# Revit family: Hager-Gamma-IP30-syst-NoHosted-CH-fr
name_source: partatom
category: Electrical Equipment
units: mm (PartAtom-declared; Revit-internal decimal feet)

## family parameters
Always vertical = Yes
Cut with Voids When Loaded = No
Panel Configuration = Two Columns, Circuits Across
Part Type = Panelboard
Room Calculation Point = No
Round Connector Dimension = Use Diameter
Shared = No
Work Plane-Based = Yes

## types (4) — shared parameters
Default Elevation = 1219 mm
EF000003 - mode de pose = EV000384 - saillie
EF000007 - couleur = EV000202 - blanc
EF000008 - largeur = 250 mm  [stored 0.82021 ft]
EF000049 - profondeur = 103 mm  [stored 0.337927 ft]
EF000116 - numéro RAL = 9010
EF000118 - avec cadre/support de montage = No
EF000339 - type de capot = EV001012 - couvercle
EF001062 - finition CEM = No
EF001088 - possibilité de montage en saillie = Yes
EF001134 - rail DIN = Yes
EF001596 - matériau du boîtier/corps = EV000139 - plastique
EF002950 - largeur en nombre de modules = 13
EF004462 - type de fermeture = EV000154 - autre
EF005474 - indice de protection (IP) = EV006410 - IP30
EF006244 - couvercle/porte transparent(e) = No
EF006306 - avec serrure = No
EF009212 - finition du couvercle = EV009916 - avec échancrure
HG000001 - nombre de colonnes = 1
HG000002 - avec porte = No
HG000003 - Gamme = Gamma
HG000005 - Epaisseur = 3 mm  [stored 0.00984252 ft]
HG000006 - Encastré = No
HG000009 - Porte à double battant = No
HG000010 - Portes asymétriques = No
HG000011 - Rangées du bas vides = No
HG000017 - Distance entre pôles = 18 mm  [stored 0.0590551 ft]
Manufacturer = Hager
Type Comments = Gamma
zero-valued in all types: EF000218 - profondeur d'encastrement, EF000332 - hauteur d'encastrement, EF000846 - largeur d'encastrement, EF001131 - profondeur intérieure, HG000007 - Nombre de colonnes vides, HG000008 - Nombre de rangées vides

## per-type parameters (varying)
| type | EF000040 - hauteur | EF000266 - nombre de rangées | EF015776 - borne de mise à la terre | EF015777 - borne à conducteur neutre | EF015941 - porte pour transmission du signal | HG000004 - Référence fabricant | Model |
| Saillie IP30 L250 H250 P103 13 Modules - GD113G | 250 mm  [stored 0.82021 ft] | 1 | Yes | Yes | Yes | GD113G | GD113G |
| Saillie IP30 L250 H375 P103 13 Modules - GD213G | 375 mm | 2 | No | No | No | GD213G | GD213G |
| Saillie IP30 L250 H500 P103 13 Modules - GD313G | 500 mm  [stored 1.64042 ft] | 3 | No | No | No | GD313G | GD313G |
| Saillie IP30 L250 H625 P103 13 Modules - GD413G | 625 mm  [stored 2.05052 ft] | 4 | No | No | No | GD413G | GD413G |

note: [stored X ft] marks values corroborated as IEEE doubles in the binary element streams (Revit-internal decimal feet)

## geometry (parser evidence)
native form markers: Sweep x13
no freeform markers — native parametric forms only
